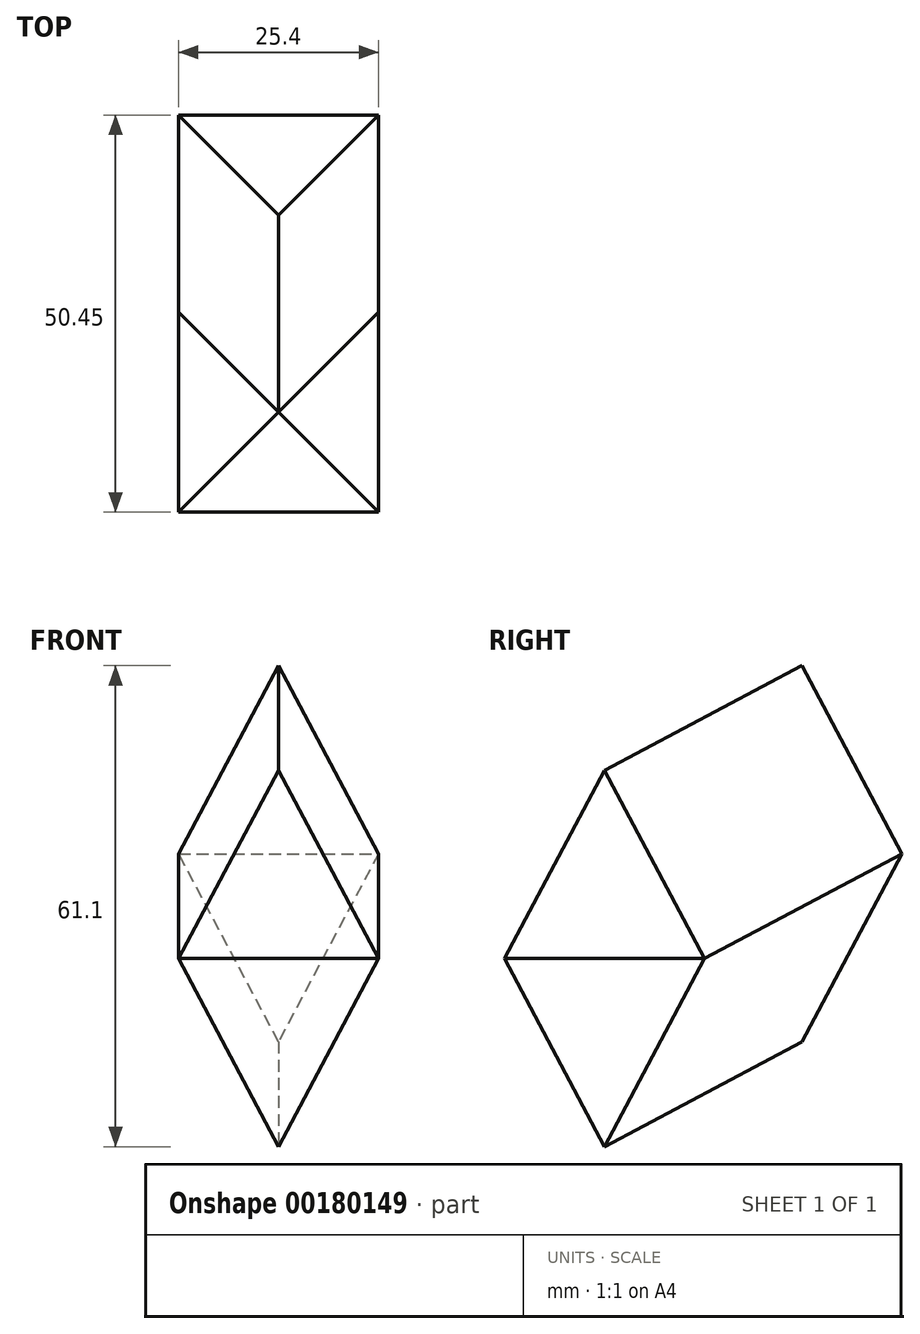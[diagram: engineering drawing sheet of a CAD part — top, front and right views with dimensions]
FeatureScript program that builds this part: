
annotation { "Feature Type Name" : "Feature", "Feature Type Description" : "" }
export const myFeature = defineFeature(function(context is Context, id is Id, definition is map)
    precondition{}
    {
        {
            var Q0;
            Q0=qCreatedBy(makeId("Top.planeOp"),FACE);
            var sketch = newSketch(context, id + "F0", { "sketchPlane" : qUnion([Q0])});
            skLineSegment(sketch, "E0.bottom", {"start": v(-12.7, 12.7) * mm, "end": v(12.7, 12.7) * mm});
            skLineSegment(sketch, "E0.top", {"start": v(-12.7, -12.7) * mm, "end": v(12.7, -12.7) * mm});
            skLineSegment(sketch, "E0.left", {"start": v(-12.7, 12.7) * mm, "end": v(-12.7, -12.7) * mm});
            skLineSegment(sketch, "E0.right", {"start": v(12.7, 12.7) * mm, "end": v(12.7, -12.7) * mm});
            skPoint(sketch, "E0.middle", {"position": v(0, 0) * mm});
            skSolve(sketch);
        }
        {
            var Q0;
            Q0=makeQuery(id+"F0.imprint","IMPRINT",FACE,{"disambiguationData":[TD([[makeQuery(id+"F0.imprint","IMPRINT",EDGE,{"derivedFrom":sQuery(id+"F0.wireOp",EDGE,"E0.bottom")}),-1.0]])]});
            extrude(context, id + "F1", {"entities" : qUnion([Q0]), "depth" : 25.4 * mm, "hasDraft" : true, "draftAngle" : 28 * degree, "draftPullDirection" : true, "hasSecondDirection" : true, "secondDirectionOppositeDirection" : true, "secondDirectionDepth" : 25.4 * mm, "hasSecondDirectionDraft" : true, "secondDirectionDraftAngle" : 28 * degree, "secondDirectionDraftPullDirection" : true});
        }
        {
            var Q0;
            Q0=makeQuery(id+"F1.split0.splitOp","SPLIT",FACE,{"derivedFrom":makeQuery(id+"F1.opExtrude","SWEPT_FACE",FACE,{"disambiguationData":[OSD([sQuery(id+"F0.wireOp",EDGE,"E0.bottom")])]}),"isFromBackBody":true});
            var Q1;
            Q1=makeQuery(id+"F1.split0.splitOp","SPLIT",FACE,{"derivedFrom":makeQuery(id+"F1.opExtrude","SWEPT_FACE",FACE,{"disambiguationData":[OSD([sQuery(id+"F0.wireOp",EDGE,"E0.bottom")])]})});
            extrude(context, id + "F2", {"entities" : qUnion([Q0, Q1]), "operationType" : NewBodyOperationType.ADD, "depth" : 28.38 * mm});
        }
    });
